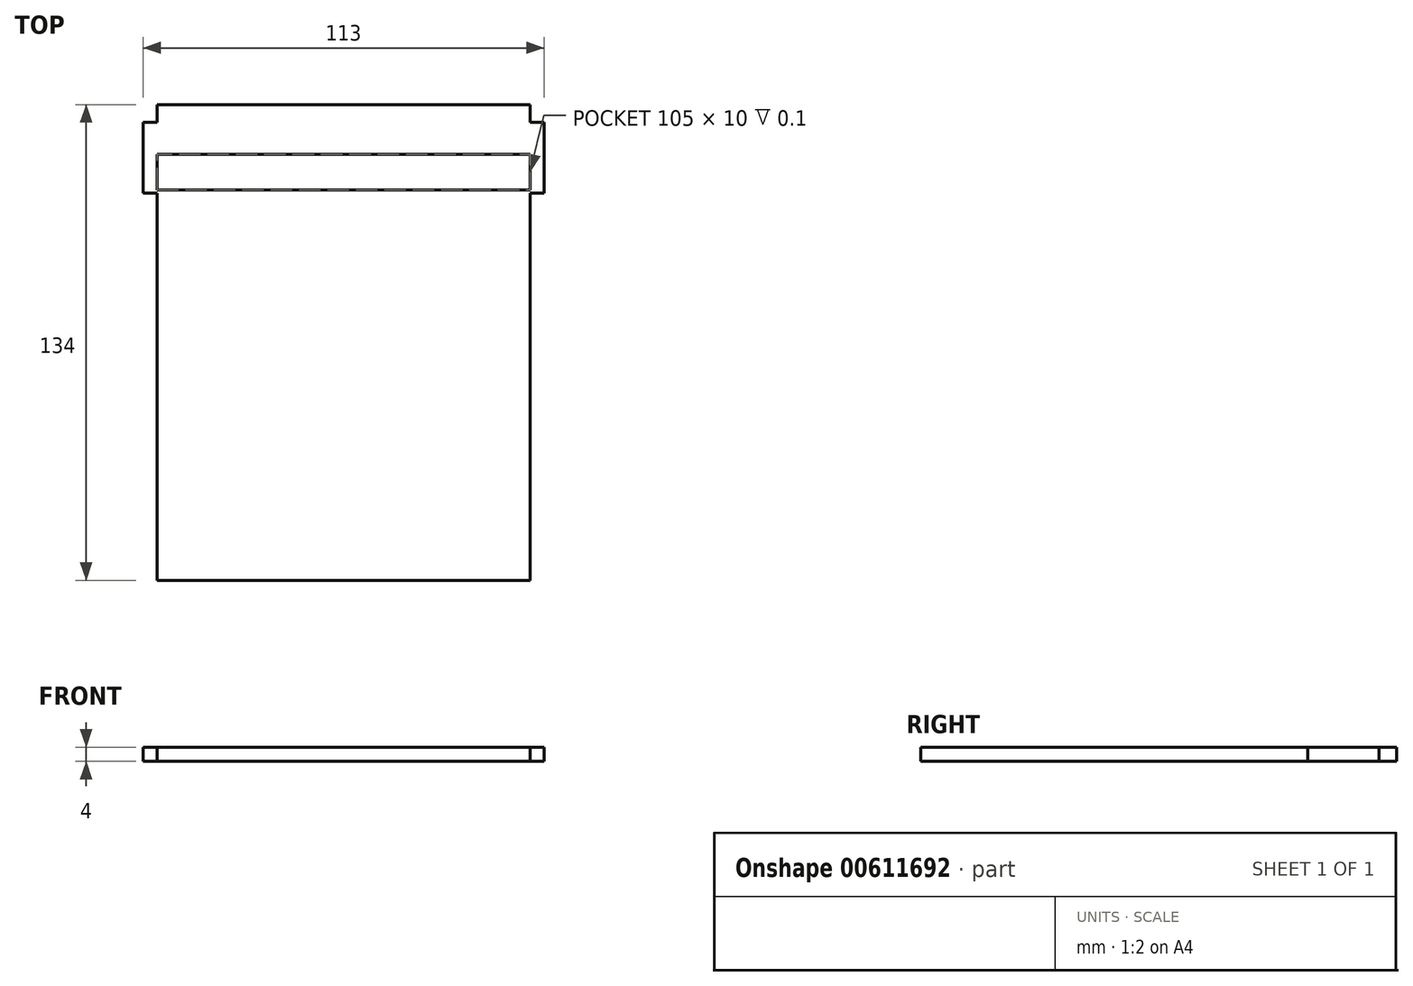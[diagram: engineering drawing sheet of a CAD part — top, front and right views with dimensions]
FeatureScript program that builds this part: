
annotation { "Feature Type Name" : "Feature", "Feature Type Description" : "" }
export const myFeature = defineFeature(function(context is Context, id is Id, definition is map)
    precondition{}
    {
        {
            var Q0;
            Q0=qCreatedBy(makeId("Top.planeOp"),FACE);
            var sketch = newSketch(context, id + "F0", { "sketchPlane" : qUnion([Q0])});
            skLineSegment(sketch, "E0.top", {"start": v(52.5, -64.5) * mm, "end": v(-52.5, -64.5) * mm});
            skLineSegment(sketch, "E0.left", {"start": v(52.5, 44.5) * mm, "end": v(52.5, -64.5) * mm});
            skLineSegment(sketch, "E0.right", {"start": v(-52.5, 44.5) * mm, "end": v(-52.5, -64.5) * mm});
            skPoint(sketch, "E0.middle", {"position": v(0, 0) * mm});
            skLineSegment(sketch, "E1.bottom", {"start": v(-52.5, 44.5) * mm, "end": v(-56.5, 44.5) * mm});
            skLineSegment(sketch, "E1.top", {"start": v(-52.5, 64.5) * mm, "end": v(-56.5, 64.5) * mm});
            skLineSegment(sketch, "E1.right", {"start": v(-56.5, 44.5) * mm, "end": v(-56.5, 64.5) * mm});
            skLineSegment(sketch, "E2.bottom", {"start": v(52.5, 64.5) * mm, "end": v(56.5, 64.5) * mm});
            skLineSegment(sketch, "E2.top", {"start": v(52.5, 44.5) * mm, "end": v(56.5, 44.5) * mm});
            skLineSegment(sketch, "E2.right", {"start": v(56.5, 64.5) * mm, "end": v(56.5, 44.5) * mm});
            skLineSegment(sketch, "E3.top", {"start": v(-52.5, 69.5) * mm, "end": v(52.5, 69.5) * mm});
            skLineSegment(sketch, "E3.left", {"start": v(-52.5, 64.5) * mm, "end": v(-52.5, 69.5) * mm});
            skLineSegment(sketch, "E3.right", {"start": v(52.5, 64.5) * mm, "end": v(52.5, 69.5) * mm});
            skSolve(sketch);
        }
        {
            var Q0;
            Q0=makeQuery(id+"F0.imprint","IMPRINT",FACE,{"disambiguationData":[TD([[makeQuery(id+"F0.imprint","IMPRINT",EDGE,{"derivedFrom":sQuery(id+"F0.wireOp",EDGE,"E0.bottom")}),1.0]])]});
            var Q1;
            Q1=makeQuery(id+"F0.imprint","IMPRINT",FACE,{"disambiguationData":[TD([[makeQuery(id+"F0.imprint","IMPRINT",EDGE,{"derivedFrom":sQuery(id+"F0.wireOp",EDGE,"E0.top")}),-1.0]])]});
            extrude(context, id + "F1", {"entities" : qUnion([Q0, Q1]), "depth" : 4 * mm, "offsetDistance" : 25 * mm});
        }
        {
            var Q0;
            Q0=makeQuery(id+"F1.opExtrude","CAP_FACE",FACE,{"disambiguationData":[OSD([sQuery(id+"F0.wireOp",EDGE,"E0.top"),sQuery(id+"F0.wireOp",EDGE,"E0.left"),sQuery(id+"F0.wireOp",EDGE,"E0.right"),sQuery(id+"F0.wireOp",EDGE,"E1.bottom"),sQuery(id+"F0.wireOp",EDGE,"E1.top"),sQuery(id+"F0.wireOp",EDGE,"E1.right"),sQuery(id+"F0.wireOp",EDGE,"E2.bottom"),sQuery(id+"F0.wireOp",EDGE,"E2.top"),sQuery(id+"F0.wireOp",EDGE,"E2.right"),sQuery(id+"F0.wireOp",EDGE,"E3.top"),sQuery(id+"F0.wireOp",EDGE,"E3.left"),sQuery(id+"F0.wireOp",EDGE,"E3.right")])],"isStart":false});
            var sketch = newSketch(context, id + "F2", { "sketchPlane" : qUnion([Q0])});
            skLineSegment(sketch, "E4.bottom", {"start": v(-52.5, 55.5) * mm, "end": v(52.5, 55.5) * mm});
            skLineSegment(sketch, "E4.top", {"start": v(-52.5, 45.5) * mm, "end": v(52.5, 45.5) * mm});
            skLineSegment(sketch, "E4.left", {"start": v(-52.5, 55.5) * mm, "end": v(-52.5, 45.5) * mm});
            skLineSegment(sketch, "E4.right", {"start": v(52.5, 55.5) * mm, "end": v(52.5, 45.5) * mm});
            skSolve(sketch);
        }
        {
            var Q0;
            Q0=makeQuery(id+"F2.imprint","IMPRINT",FACE,{"disambiguationData":[TD([[makeQuery(id+"F2.imprint","IMPRINT",EDGE,{"derivedFrom":sQuery(id+"F2.wireOp",EDGE,"E4.bottom")}),-1.0]])]});
            extrude(context, id + "F3", {"entities" : qUnion([Q0]), "operationType" : NewBodyOperationType.REMOVE, "oppositeDirection" : true, "depth" : 0.1 * mm, "offsetDistance" : 25 * mm});
        }
    });
